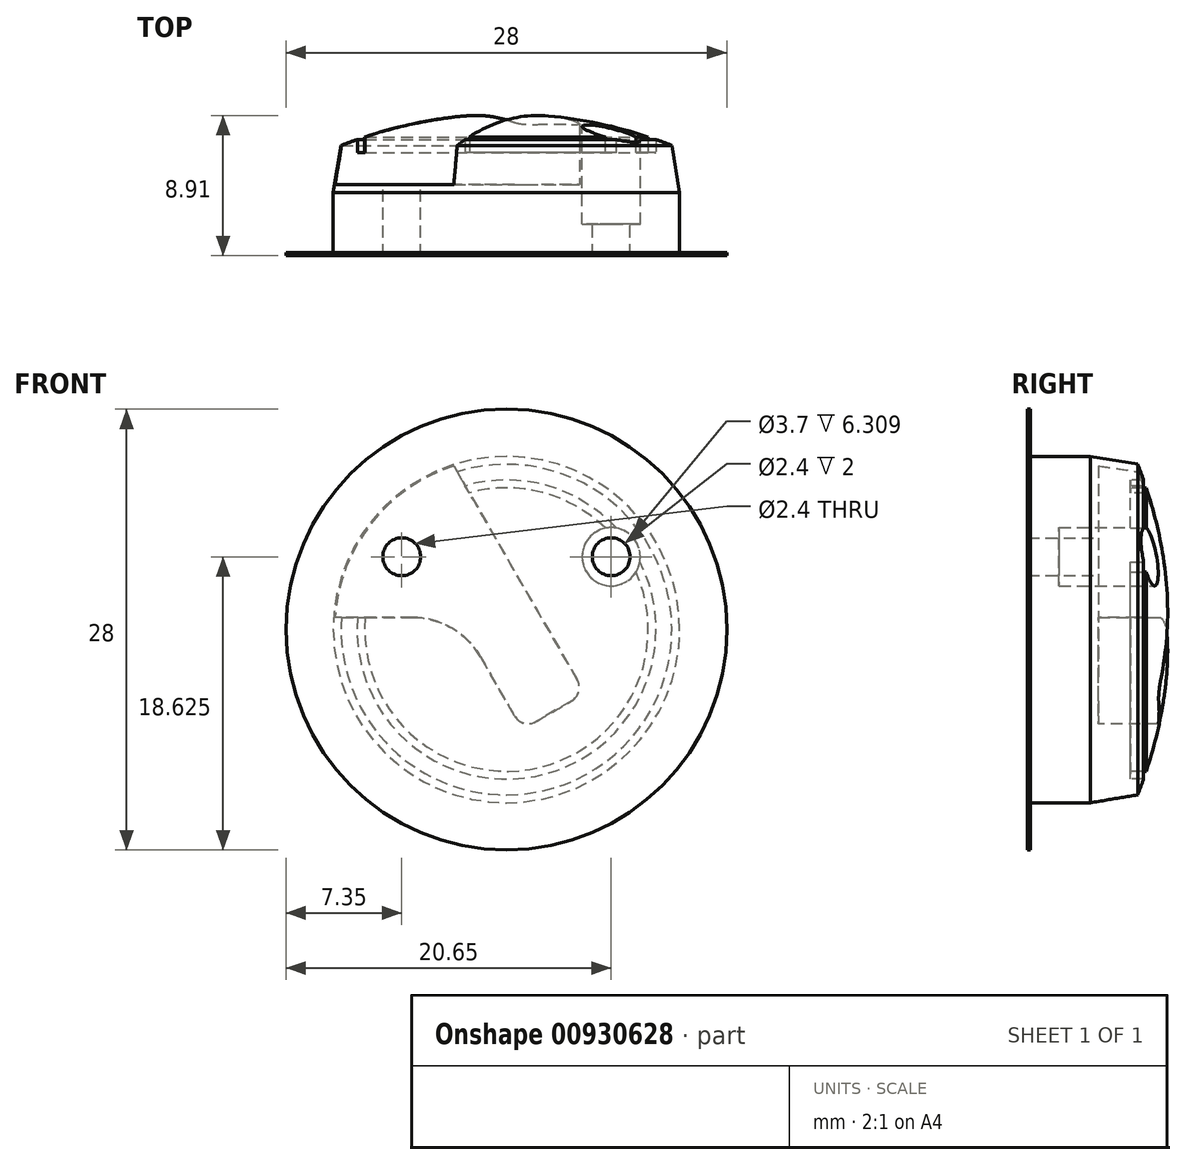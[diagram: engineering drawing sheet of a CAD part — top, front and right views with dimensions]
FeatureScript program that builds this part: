
annotation { "Feature Type Name" : "Feature", "Feature Type Description" : "" }
export const myFeature = defineFeature(function(context is Context, id is Id, definition is map)
    precondition{}
    {
        {
            var Q0;
            Q0=qCreatedBy(makeId("Top.planeOp"),FACE);
            var sketch = newSketch(context, id + "F0", { "sketchPlane" : qUnion([Q0])});
            skLineSegment(sketch, "E0", {"start": v(0, 0) * mm, "end": v(0, 9) * mm});
            skLineSegment(sketch, "E1", {"start": v(0, 0) * mm, "end": v(11, 0) * mm});
            skLineSegment(sketch, "E2", {"start": v(11, 0) * mm, "end": v(11, 4) * mm});
            skLineSegment(sketch, "E3", {"start": v(11, 4) * mm, "end": v(10.5, 7) * mm});
            skArc(sketch, "E4", {"start": v(10.5, 7) * mm, "mid": v(10, 7.2) * mm, "end": v(9.5, 7.37) * mm});
            skLineSegment(sketch, "E5", {"start": v(0, 9) * mm, "end": v(11, 9) * mm, "construction": true});
            skLineSegment(sketch, "E6", {"start": v(11, 9) * mm, "end": v(11, 0) * mm, "construction": true});
            skLineSegment(sketch, "E7", {"start": v(9, 7.54) * mm, "end": v(9, 6.54) * mm});
            skLineSegment(sketch, "E8", {"start": v(9, 6.54) * mm, "end": v(9.5, 6.54) * mm});
            skLineSegment(sketch, "E9", {"start": v(9.5, 6.54) * mm, "end": v(9.5, 7.37) * mm});
            skArc(sketch, "E10.trimOffspring", {"start": v(9, 7.54) * mm, "mid": v(4.56, 8.63) * mm, "end": v(0, 9) * mm});
            skSolve(sketch);
        }
        {
            var Q0;
            Q0=qSketchRegion(id+"F0",true);
            var Q1;
            Q1=sQuery(id+"F0.wireOp",EDGE,"E0");
            revolve(context, id + "F1", {"entities" : qUnion([Q0]), "axis" : qUnion([Q1]), "revolveType" : RevolveType.FULL});
        }
        {
            var Q0;
            Q0=qCreatedBy(makeId("Front.planeOp"),FACE);
            cPlane(context, id + "F2", {"entities" : qUnion([Q0]), "cplaneType" : CPlaneType.OFFSET, "offset" : 9 * mm, "oppositeDirection" : true, "width" : 150 * mm, "height" : 150 * mm});
        }
        {
            var Q0;
            Q0=qCreatedBy(id+"F2.planeOp",FACE);
            var sketch = newSketch(context, id + "F3", { "sketchPlane" : qUnion([Q0])});
            skCircle(sketch, "E11", {"center": v(6.65, 4.62) * mm, "radius": 1.85 * mm});
            skSolve(sketch);
        }
        {
            var Q0;
            Q0=qSketchRegion(id+"F3",true);
            extrude(context, id + "F4", {"entities" : qUnion([Q0]), "operationType" : NewBodyOperationType.REMOVE, "depth" : 7 * mm, "offsetDistance" : 25 * mm});
        }
        {
            var Q0;
            Q0=makeQuery(id+"F4.boolean.opBoolean","COPY",FACE,{"derivedFrom":makeQuery(id+"F4.opExtrude","CAP_FACE",FACE,{"disambiguationData":[OSD([sQuery(id+"F3.wireOp",EDGE,"E11")])],"isStart":false})});
            var sketch = newSketch(context, id + "F5", { "sketchPlane" : qUnion([Q0])});
            skCircle(sketch, "E12", {"center": v(-6.65, 4.62) * mm, "radius": 1.2 * mm});
            skSolve(sketch);
        }
        {
            var Q0;
            Q0=qSketchRegion(id+"F5",true);
            extrude(context, id + "F6", {"entities" : qUnion([Q0]), "operationType" : NewBodyOperationType.REMOVE, "endBound" : BoundingType.UP_TO_NEXT, "oppositeDirection" : true, "depth" : 25 * mm, "offsetDistance" : 25 * mm});
        }
        {
            var Q0;
            Q0=qCreatedBy(id+"F2.planeOp",FACE);
            var sketch = newSketch(context, id + "F7", { "sketchPlane" : qUnion([Q0])});
            skLineSegment(sketch, "E13", {"start": v(5.5, -9.53) * mm, "end": v(-5.5, 9.53) * mm, "construction": true});
            skLineSegment(sketch, "E14", {"start": v(-3.39, 10.47) * mm, "end": v(5, -4.05) * mm});
            skLineSegment(sketch, "E15", {"start": v(1, -6.35) * mm, "end": v(-3.1, 0.78) * mm});
            skArc(sketch, "E16", {"start": v(-3.39, 10.47) * mm, "mid": v(-8.66, 6.78) * mm, "end": v(-10.97, 0.77) * mm});
            skLineSegment(sketch, "E17", {"start": v(5, -4.05) * mm, "end": v(1, -6.35) * mm});
            skLineSegment(sketch, "E18", {"start": v(-3.1, 0.78) * mm, "end": v(-10.97, 0.77) * mm});
            skSolve(sketch);
        }
        {
            var Q0;
            Q0=qSketchRegion(id+"F7",true);
            extrude(context, id + "F8", {"entities" : qUnion([Q0]), "operationType" : NewBodyOperationType.REMOVE, "depth" : 4.5 * mm, "offsetDistance" : 25 * mm});
        }
        {
            var Q0;
            Q0=makeQuery(id+"F8.boolean.opBoolean","COPY",EDGE,{"derivedFrom":makeQuery(id+"F8.opExtrude","SWEPT_EDGE",EDGE,{"disambiguationData":[OSD([sQuery(id+"F7.wireOp",EDGE,"E14"),sQuery(id+"F7.wireOp",EDGE,"E17")])]})});
            var Q1;
            Q1=makeQuery(id+"F8.boolean.opBoolean","COPY",EDGE,{"derivedFrom":makeQuery(id+"F8.opExtrude","SWEPT_EDGE",EDGE,{"disambiguationData":[OSD([sQuery(id+"F7.wireOp",EDGE,"E15"),sQuery(id+"F7.wireOp",EDGE,"E17")])]})});
            fillet(context, id + "F9", {"entities" : qUnion([Q0, Q1]), "radius" : 1 * mm, "tangentPropagation" : true, "allowEdgeOverflow" : false});
        }
        {
            var Q0;
            Q0=makeQuery(id+"F8.boolean.opBoolean","COPY",FACE,{"derivedFrom":makeQuery(id+"F8.opExtrude","CAP_FACE",FACE,{"disambiguationData":[OSD([sQuery(id+"F7.wireOp",EDGE,"E14"),sQuery(id+"F7.wireOp",EDGE,"E15"),sQuery(id+"F7.wireOp",EDGE,"E16"),sQuery(id+"F7.wireOp",EDGE,"E17"),sQuery(id+"F7.wireOp",EDGE,"E18")])],"isStart":false})});
            var sketch = newSketch(context, id + "F10", { "sketchPlane" : qUnion([Q0])});
            skCircle(sketch, "E19", {"center": v(6.65, 4.62) * mm, "radius": 1.2 * mm});
            skSolve(sketch);
        }
        {
            var Q0;
            Q0=qSketchRegion(id+"F10",true);
            extrude(context, id + "F11", {"entities" : qUnion([Q0]), "operationType" : NewBodyOperationType.REMOVE, "endBound" : BoundingType.UP_TO_NEXT, "oppositeDirection" : true, "depth" : 25 * mm, "offsetDistance" : 25 * mm});
        }
        {
            var Q0;
            Q0=makeQuery(id+"F8.boolean.opBoolean","COPY",EDGE,{"derivedFrom":makeQuery(id+"F8.opExtrude","SWEPT_EDGE",EDGE,{"disambiguationData":[OSD([sQuery(id+"F7.wireOp",EDGE,"E15"),sQuery(id+"F7.wireOp",EDGE,"E18")])]})});
            fillet(context, id + "F12", {"entities" : qUnion([Q0]), "radius" : 5 * mm, "tangentPropagation" : true, "allowEdgeOverflow" : false});
        }
        {
            var Q0;
            Q0=makeQuery(id+"F1.opRevolve","SWEPT_FACE",FACE,{"disambiguationData":[OSD([sQuery(id+"F0.wireOp",EDGE,"E1")])]});
            var sketch = newSketch(context, id + "F13", { "sketchPlane" : qUnion([Q0])});
            skCircle(sketch, "E20", {"center": v(0, 0) * mm, "radius": 14 * mm});
            skCircle(sketch, "E21", {"center": v(0, 0) * mm, "radius": 11 * mm});
            skSolve(sketch);
        }
        {
            var Q0;
            Q0=qSketchRegion(id+"F13",true);
            extrude(context, id + "F14", {"entities" : qUnion([Q0]), "operationType" : NewBodyOperationType.ADD, "oppositeDirection" : true, "depth" : 0.2 * mm, "offsetDistance" : 25 * mm});
        }
    });
